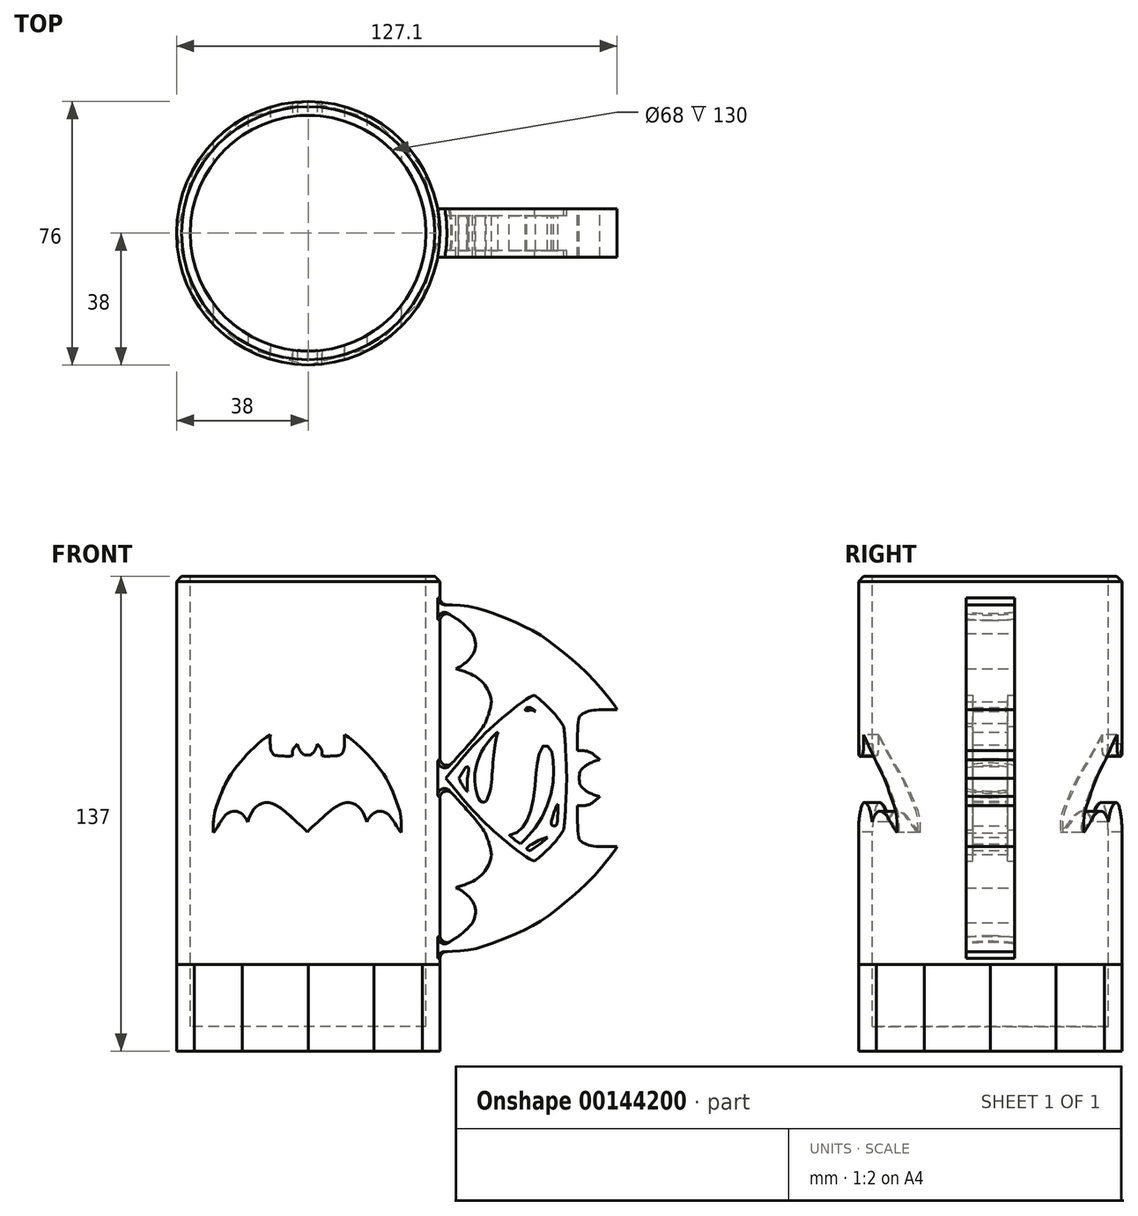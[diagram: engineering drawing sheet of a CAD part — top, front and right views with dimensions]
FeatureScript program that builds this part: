
annotation { "Feature Type Name" : "Feature", "Feature Type Description" : "" }
export const myFeature = defineFeature(function(context is Context, id is Id, definition is map)
    precondition{}
    {
        {
            var Q0;
            Q0=qCreatedBy(makeId("Top.planeOp"),FACE);
            var sketch = newSketch(context, id + "F0", { "sketchPlane" : qUnion([Q0])});
            skCircle(sketch, "E0", {"center": v(0, 0) * mm, "radius": 38 * mm});
            skSolve(sketch);
        }
        {
            var Q0;
            Q0=qSketchRegion(id+"F0",true);
            extrude(context, id + "F1", {"entities" : qUnion([Q0]), "depth" : 137 * mm});
        }
        {
            var Q0;
            Q0=makeQuery(id+"F1.opExtrude","CAP_FACE",FACE,{"disambiguationData":[OSD([sQuery(id+"F0.wireOp",EDGE,"E0")])],"isStart":false});
            var sketch = newSketch(context, id + "F2", { "sketchPlane" : qUnion([Q0])});
            skCircle(sketch, "E1", {"center": v(0, 0) * mm, "radius": 34 * mm});
            skSolve(sketch);
        }
        {
            var Q0;
            Q0=qSketchRegion(id+"F2",true);
            extrude(context, id + "F3", {"entities" : qUnion([Q0]), "operationType" : NewBodyOperationType.REMOVE, "oppositeDirection" : true, "depth" : 130 * mm});
        }
        {
            var Q0;
            Q0=qCreatedBy(makeId("Front.planeOp"),FACE);
            var sketch = newSketch(context, id + "F4", { "sketchPlane" : qUnion([Q0])});
            skFitSpline(sketch, "E2", {"points": [v(36.9, 128.73) * mm, v(42.12, 128.73) * mm, v(47.93, 128) * mm, v(54.17, 125.97) * mm, v(60.56, 123.36) * mm, v(67.67, 119.58) * mm, v(74.93, 113.92) * mm, v(82.05, 107.39) * mm, v(88.87, 98.97) * mm, v(89.1, 98.44) * mm], "startDerivative": vector(51.79, 1.09) * mm, "endDerivative": vector(2.7, -11.12) * mm});
            skFitSpline(sketch, "E3", {"points": [v(89.1, 98.44) * mm, v(83.25, 98.44) * mm, v(80.58, 97.98) * mm, v(78.7, 96.95) * mm, v(78.04, 95.83) * mm, v(77.66, 86.63) * mm], "startDerivative": vector(-27.8, 0.53) * mm, "endDerivative": vector(0.96, -37) * mm});
            skFitSpline(sketch, "E4", {"points": [v(77.66, 86.63) * mm, v(79.5, 86.63) * mm, v(81.03, 86.36) * mm, v(82.92, 85.1) * mm, v(84.15, 84.06) * mm], "startDerivative": vector(6.72, 0.3) * mm, "endDerivative": vector(4.9, -4.18) * mm});
            skFitSpline(sketch, "E5", {"points": [v(84.15, 84.06) * mm, v(81.63, 83.24) * mm, v(79.99, 82.28) * mm, v(78.53, 80.8) * mm, v(78.19, 78.74) * mm], "startDerivative": vector(-7.25, -1.04) * mm, "endDerivative": vector(-0.08, -9.17) * mm});
            skFitSpline(sketch, "E6", {"points": [v(36.9, 128.73) * mm, v(43.3, 124.4) * mm, v(46.88, 121.41) * mm, v(48.14, 116) * mm, v(44.69, 111.5) * mm, v(42.61, 110.37) * mm], "startDerivative": vector(16.64, -13.44) * mm, "endDerivative": vector(-14.87, -5.9) * mm});
            skFitSpline(sketch, "E7", {"points": [v(42.61, 110.37) * mm, v(44.83, 109.6) * mm, v(49.77, 106.88) * mm, v(52.87, 100.78) * mm, v(51.04, 94.56) * mm, v(44.19, 86.1) * mm, v(39.39, 80.85) * mm, v(37.25, 78.74) * mm], "startDerivative": vector(23.87, -9.84) * mm, "endDerivative": vector(-19.45, -17.88) * mm});
            skLineSegment(sketch, "E8", {"start": v(33.29, 78.74) * mm, "end": v(88.65, 78.74) * mm, "construction": true});
            skFitSpline(sketch, "E9.MirrorCS", {"points": [v(84.15, 73.42) * mm, v(81.63, 74.24) * mm, v(79.99, 75.2) * mm, v(78.53, 76.68) * mm, v(78.19, 78.74) * mm], "startDerivative": vector(-7.25, 1.04) * mm, "endDerivative": vector(-0.08, 9.17) * mm});
            skFitSpline(sketch, "E10.MirrorCS", {"points": [v(77.66, 70.85) * mm, v(79.5, 70.85) * mm, v(81.03, 71.13) * mm, v(82.92, 72.4) * mm, v(84.15, 73.42) * mm], "startDerivative": vector(6.72, -0.3) * mm, "endDerivative": vector(4.9, 4.18) * mm});
            skFitSpline(sketch, "E11.MirrorCS", {"points": [v(89.1, 59.04) * mm, v(83.25, 59.04) * mm, v(80.58, 59.5) * mm, v(78.7, 60.53) * mm, v(78.04, 61.65) * mm, v(77.66, 70.85) * mm], "startDerivative": vector(-27.8, -0.53) * mm, "endDerivative": vector(0.96, 37) * mm});
            skFitSpline(sketch, "E12.MirrorCS", {"points": [v(36.9, 28.75) * mm, v(42.12, 28.75) * mm, v(47.93, 29.48) * mm, v(54.17, 31.51) * mm, v(60.56, 34.12) * mm, v(67.67, 37.9) * mm, v(74.93, 43.56) * mm, v(82.05, 50.1) * mm, v(88.87, 58.52) * mm, v(89.1, 59.04) * mm], "startDerivative": vector(51.79, -1.09) * mm, "endDerivative": vector(2.7, 11.12) * mm});
            skFitSpline(sketch, "E13.MirrorCS", {"points": [v(36.9, 28.75) * mm, v(43.3, 33.07) * mm, v(46.88, 36.07) * mm, v(48.14, 41.49) * mm, v(44.69, 45.98) * mm, v(42.61, 47.12) * mm], "startDerivative": vector(16.64, 13.44) * mm, "endDerivative": vector(-14.87, 5.9) * mm});
            skFitSpline(sketch, "E14.MirrorCS", {"points": [v(42.61, 47.12) * mm, v(44.83, 47.89) * mm, v(49.77, 50.6) * mm, v(52.87, 56.7) * mm, v(51.04, 62.92) * mm, v(44.19, 71.4) * mm, v(39.39, 76.63) * mm, v(37.25, 78.74) * mm], "startDerivative": vector(23.87, 9.84) * mm, "endDerivative": vector(-19.45, 17.88) * mm});
            skLineSegment(sketch, "E15", {"start": v(64.5, 49.68) * mm, "end": v(64.5, 113.06) * mm, "construction": true});
            skFitSpline(sketch, "E16", {"points": [v(74.58, 78.74) * mm, v(74.04, 90.2) * mm, v(73.7, 93.64) * mm], "startDerivative": vector(-0.8, 20.33) * mm, "endDerivative": vector(-0.95, 8.3) * mm});
            skFitSpline(sketch, "E17", {"points": [v(73.7, 93.64) * mm, v(70.4, 98.01) * mm, v(65.3, 102.65) * mm], "startDerivative": vector(-6.4, 9.4) * mm, "endDerivative": vector(-3.05, 1.66) * mm});
            skFitSpline(sketch, "E18", {"points": [v(65.3, 102.65) * mm, v(59.66, 99.1) * mm, v(49.84, 90.46) * mm, v(39.71, 78.74) * mm], "startDerivative": vector(-13.82, -2.57) * mm, "endDerivative": vector(-25.21, -31.02) * mm});
            skFitSpline(sketch, "E19", {"points": [v(45.95, 74.86) * mm, v(45.9, 78.74) * mm, v(46.28, 81.04) * mm, v(45.73, 82.1) * mm], "startDerivative": vector(-0.69, 9.3) * mm, "endDerivative": vector(-5.98, 2.33) * mm});
            skFitSpline(sketch, "E20", {"points": [v(45.73, 82.1) * mm, v(44.59, 80.57) * mm, v(43.51, 78.74) * mm], "startDerivative": vector(-3.02, -2.78) * mm, "endDerivative": vector(-1.95, -3.79) * mm});
            skFitSpline(sketch, "E21", {"points": [v(43.51, 78.74) * mm, v(44.28, 77.1) * mm, v(45.08, 75.82) * mm, v(45.95, 74.86) * mm], "startDerivative": vector(0.56, -4.35) * mm, "endDerivative": vector(2.23, -1.28) * mm});
            skFitSpline(sketch, "E22.MirrorCS", {"points": [v(74.58, 78.74) * mm, v(74.04, 67.3) * mm, v(73.7, 63.85) * mm], "startDerivative": vector(-0.8, -20.33) * mm, "endDerivative": vector(-0.95, -8.3) * mm});
            skFitSpline(sketch, "E23.MirrorCS", {"points": [v(73.7, 63.85) * mm, v(70.4, 59.47) * mm, v(65.3, 54.83) * mm], "startDerivative": vector(-6.4, -9.4) * mm, "endDerivative": vector(-3.05, -1.66) * mm});
            skFitSpline(sketch, "E24.MirrorCS", {"points": [v(65.3, 54.83) * mm, v(59.66, 58.4) * mm, v(49.84, 67.02) * mm, v(39.71, 78.74) * mm], "startDerivative": vector(-13.82, 2.57) * mm, "endDerivative": vector(-25.21, 31.02) * mm});
            skFitSpline(sketch, "E25", {"points": [v(54.78, 92.08) * mm, v(54.1, 89.74) * mm, v(53.36, 83.81) * mm, v(52.59, 75.72) * mm, v(51.31, 72.04) * mm], "startDerivative": vector(-3.91, -11.71) * mm, "endDerivative": vector(-7.77, -13.72) * mm});
            skFitSpline(sketch, "E26", {"points": [v(51.31, 72.04) * mm, v(50.45, 71.85) * mm, v(49.56, 72.25) * mm, v(48.61, 74.4) * mm, v(48.12, 77.19) * mm, v(48.12, 80.34) * mm, v(49.23, 84.76) * mm, v(51.7, 89) * mm, v(53.85, 91.39) * mm, v(54.78, 92.08) * mm], "startDerivative": vector(-12.82, -4.34) * mm, "endDerivative": vector(11.18, 7.53) * mm});
            skFitSpline(sketch, "E27", {"points": [v(65.56, 98.05) * mm, v(64.5, 98.4) * mm, v(63.24, 98.23) * mm, v(62.59, 98.42) * mm, v(63.64, 99.17) * mm, v(65.56, 98.05) * mm]});
            skFitSpline(sketch, "E28", {"points": [v(72, 71.25) * mm, v(71.96, 68.06) * mm, v(71.7, 65.44) * mm, v(71.02, 64.97) * mm, v(70.23, 65.23) * mm, v(70.71, 68.28) * mm, v(72, 71.25) * mm]});
            skFitSpline(sketch, "E29", {"points": [v(68.95, 61.62) * mm, v(66.19, 59.31) * mm, v(64.16, 57.89) * mm, v(63.51, 57.95) * mm, v(63.07, 58.36) * mm, v(63.99, 59.34) * mm, v(66.8, 60.93) * mm, v(68.95, 61.62) * mm]});
            skFitSpline(sketch, "E30", {"points": [v(61.22, 59.77) * mm, v(60.27, 60.5) * mm, v(57.96, 62.14) * mm, v(59.38, 62.77) * mm, v(61.38, 64.03) * mm, v(62.75, 65.82) * mm, v(64.04, 68.72) * mm, v(65.11, 73.92) * mm, v(65.72, 80.16) * mm, v(66.14, 83.44) * mm, v(66.95, 86.55) * mm, v(68.14, 88.3) * mm, v(69.2, 87.92) * mm, v(70.19, 86.6) * mm, v(70.64, 84.34) * mm, v(70.77, 80.26) * mm, v(70.27, 75.47) * mm, v(68.59, 70.03) * mm, v(66.14, 65.32) * mm, v(61.88, 60.3) * mm, v(61.22, 59.77) * mm]});
            skLineSegment(sketch, "E31", {"start": v(0, 0) * mm, "end": v(0, 137) * mm, "construction": true});
            skLineSegment(sketch, "E32", {"start": v(0, 137) * mm, "end": v(38, 137) * mm, "construction": true});
            skLineSegment(sketch, "E33", {"start": v(38, 137) * mm, "end": v(38, 117) * mm, "construction": true});
            skArc(sketch, "E34", {"start": v(51.04, 94.56) * mm, "mid": v(52.37, 110.83) * mm, "end": v(43.3, 124.4) * mm});
            skArc(sketch, "E35", {"start": v(43.3, 33.07) * mm, "mid": v(52.37, 46.65) * mm, "end": v(51.04, 62.92) * mm});
            skSolve(sketch);
        }
        {
            var Q0;
            Q0=qSketchRegion(id+"F4",true);
            extrude(context, id + "F5", {"entities" : qUnion([Q0]), "operationType" : NewBodyOperationType.ADD, "endBound" : BoundingType.SYMMETRIC, "depth" : 14 * mm});
        }
        {
            var Q0;
            Q0=makeQuery(id+"F4.imprint","IMPRINT",FACE,{"disambiguationData":[TD([[makeQuery(id+"F4.imprint","IMPRINT",EDGE,{"derivedFrom":sQuery(id+"F4.wireOp",EDGE,"E16")}),1.0]])]});
            extrude(context, id + "F6", {"entities" : qUnion([Q0]), "operationType" : NewBodyOperationType.ADD, "endBound" : BoundingType.SYMMETRIC, "depth" : 10 * mm});
        }
        {
            var Q0;
            Q0=makeQuery(id+"F5.boolean.opBoolean","INTERSECT",EDGE,{"derivedFrom":[makeQuery(id+"F1.opExtrude","SWEPT_FACE",FACE,{"disambiguationData":[OSD([sQuery(id+"F0.wireOp",EDGE,"E0")])]}),makeQuery(id+"F5.opExtrude","SWEPT_FACE",FACE,{"disambiguationData":[OSD([sQuery(id+"F4.wireOp",EDGE,"E2")])]})]});
            var Q1;
            Q1=makeQuery(id+"F5.boolean.opBoolean","INTERSECT",EDGE,{"derivedFrom":[makeQuery(id+"F1.opExtrude","SWEPT_FACE",FACE,{"disambiguationData":[OSD([sQuery(id+"F0.wireOp",EDGE,"E0")])]}),makeQuery(id+"F5.opExtrude","SWEPT_FACE",FACE,{"disambiguationData":[OSD([sQuery(id+"F4.wireOp",EDGE,"E6")])]})]});
            var Q2;
            Q2=makeQuery(id+"F5.boolean.opBoolean","INTERSECT",EDGE,{"derivedFrom":[makeQuery(id+"F1.opExtrude","SWEPT_FACE",FACE,{"disambiguationData":[OSD([sQuery(id+"F0.wireOp",EDGE,"E0")])]}),makeQuery(id+"F5.opExtrude","SWEPT_FACE",FACE,{"disambiguationData":[OSD([sQuery(id+"F4.wireOp",EDGE,"E13.MirrorCS")])]})]});
            var Q3;
            Q3=makeQuery(id+"F5.boolean.opBoolean","INTERSECT",EDGE,{"derivedFrom":[makeQuery(id+"F1.opExtrude","SWEPT_FACE",FACE,{"disambiguationData":[OSD([sQuery(id+"F0.wireOp",EDGE,"E0")])]}),makeQuery(id+"F5.opExtrude","SWEPT_FACE",FACE,{"disambiguationData":[OSD([sQuery(id+"F4.wireOp",EDGE,"E14.MirrorCS")])]})]});
            var Q4;
            Q4=makeQuery(id+"F5.boolean.opBoolean","INTERSECT",EDGE,{"derivedFrom":[makeQuery(id+"F1.opExtrude","SWEPT_FACE",FACE,{"disambiguationData":[OSD([sQuery(id+"F0.wireOp",EDGE,"E0")])]}),makeQuery(id+"F5.opExtrude","SWEPT_FACE",FACE,{"disambiguationData":[OSD([sQuery(id+"F4.wireOp",EDGE,"E12.MirrorCS")])]})]});
            var Q5;
            Q5=makeQuery(id+"F5.boolean.opBoolean","INTERSECT",EDGE,{"derivedFrom":[makeQuery(id+"F1.opExtrude","SWEPT_FACE",FACE,{"disambiguationData":[OSD([sQuery(id+"F0.wireOp",EDGE,"E0")])]}),makeQuery(id+"F5.opExtrude","SWEPT_FACE",FACE,{"disambiguationData":[OSD([sQuery(id+"F4.wireOp",EDGE,"E7")])]})]});
            fillet(context, id + "F7", {"entities" : qUnion([Q0, Q1, Q2, Q3, Q4, Q5]), "radius" : 2 * mm, "tangentPropagation" : true, "allowEdgeOverflow" : false});
        }
        {
            var Q0;
            Q0=makeQuery(id+"F1.opExtrude","CAP_EDGE",EDGE,{"disambiguationData":[OSD([sQuery(id+"F0.wireOp",EDGE,"E0")])],"isStart":false});
            chamfer(context, id + "F8", {"entities" : qUnion([Q0]), "width" : 1.5 * mm, "tangentPropagation" : true});
        }
        {
            var Q0;
            Q0=makeQuery(id+"F1.opExtrude","CAP_FACE",FACE,{"disambiguationData":[OSD([sQuery(id+"F0.wireOp",EDGE,"E0")])],"isStart":true});
            var sketch = newSketch(context, id + "F9", { "sketchPlane" : qUnion([Q0])});
            skLineSegment(sketch, "E36", {"start": v(0, 38) * mm, "end": v(0, 0) * mm, "construction": true});
            skLineSegment(sketch, "E37", {"start": v(0, 0) * mm, "end": v(-38, 0) * mm, "construction": true});
            skLineSegment(sketch, "E38", {"start": v(0, 0) * mm, "end": v(-32.9, 19) * mm, "construction": true});
            skLineSegment(sketch, "E39", {"start": v(-38, 0) * mm, "end": v(-32.9, 19) * mm});
            skLineSegment(sketch, "E40.1.0", {"start": v(-32.9, -19) * mm, "end": v(-38, 0) * mm});
            skLineSegment(sketch, "E40.2.0", {"start": v(-19, -32.9) * mm, "end": v(-32.9, -19) * mm});
            skLineSegment(sketch, "E40.3.0", {"start": v(0, -38) * mm, "end": v(-19, -32.9) * mm});
            skLineSegment(sketch, "E40.4.0", {"start": v(19, -32.9) * mm, "end": v(0, -38) * mm});
            skLineSegment(sketch, "E40.5.0", {"start": v(32.9, -19) * mm, "end": v(19, -32.9) * mm});
            skLineSegment(sketch, "E40.6.0", {"start": v(38, 0) * mm, "end": v(32.9, -19) * mm});
            skLineSegment(sketch, "E40.7.0", {"start": v(32.9, 19) * mm, "end": v(38, 0) * mm});
            skLineSegment(sketch, "E40.8.0", {"start": v(19, 32.9) * mm, "end": v(32.9, 19) * mm});
            skLineSegment(sketch, "E40.9.0", {"start": v(0, 38) * mm, "end": v(19, 32.9) * mm});
            skLineSegment(sketch, "E40.10.0", {"start": v(-19, 32.9) * mm, "end": v(0, 38) * mm});
            skLineSegment(sketch, "E40.11.0", {"start": v(-32.9, 19) * mm, "end": v(-19, 32.9) * mm});
            skPoint(sketch, "E40.center", {"position": v(0, 0) * mm});
            skLineSegment(sketch, "E41", {"start": v(0, 0) * mm, "end": v(-19, 32.9) * mm, "construction": true});
            skSolve(sketch);
        }
        {
            var Q0;
            {var subQ0=sQuery(id+"F9.wireOp",EDGE,"E40.11.0");Q0=makeQuery(id+"F9.imprint","IMPRINT",FACE,{"disambiguationData":[TD([[makeQuery(id+"F9.imprint","IMPRINT",EDGE,{"derivedFrom":subQ0}),1.0]])]});}
            var Q1;
            {var subQ0=sQuery(id+"F9.wireOp",EDGE,"E39");Q1=makeQuery(id+"F9.imprint","IMPRINT",FACE,{"disambiguationData":[TD([[makeQuery(id+"F9.imprint","IMPRINT",EDGE,{"derivedFrom":subQ0}),1.0]])]});}
            var Q2;
            {var subQ0=sQuery(id+"F9.wireOp",EDGE,"E40.10.0");Q2=makeQuery(id+"F9.imprint","IMPRINT",FACE,{"disambiguationData":[TD([[makeQuery(id+"F9.imprint","IMPRINT",EDGE,{"derivedFrom":subQ0}),1.0]])]});}
            var Q3;
            {var subQ0=sQuery(id+"F9.wireOp",EDGE,"E40.9.0");Q3=makeQuery(id+"F9.imprint","IMPRINT",FACE,{"disambiguationData":[TD([[makeQuery(id+"F9.imprint","IMPRINT",EDGE,{"derivedFrom":subQ0}),1.0]])]});}
            var Q4;
            {var subQ0=sQuery(id+"F9.wireOp",EDGE,"E40.8.0");Q4=makeQuery(id+"F9.imprint","IMPRINT",FACE,{"disambiguationData":[TD([[makeQuery(id+"F9.imprint","IMPRINT",EDGE,{"derivedFrom":subQ0}),1.0]])]});}
            var Q5;
            {var subQ0=sQuery(id+"F9.wireOp",EDGE,"E40.7.0");Q5=makeQuery(id+"F9.imprint","IMPRINT",FACE,{"disambiguationData":[TD([[makeQuery(id+"F9.imprint","IMPRINT",EDGE,{"derivedFrom":subQ0}),1.0]])]});}
            var Q6;
            {var subQ0=sQuery(id+"F9.wireOp",EDGE,"E40.6.0");Q6=makeQuery(id+"F9.imprint","IMPRINT",FACE,{"disambiguationData":[TD([[makeQuery(id+"F9.imprint","IMPRINT",EDGE,{"derivedFrom":subQ0}),1.0]])]});}
            var Q7;
            {var subQ0=sQuery(id+"F9.wireOp",EDGE,"E40.5.0");Q7=makeQuery(id+"F9.imprint","IMPRINT",FACE,{"disambiguationData":[TD([[makeQuery(id+"F9.imprint","IMPRINT",EDGE,{"derivedFrom":subQ0}),1.0]])]});}
            var Q8;
            {var subQ0=sQuery(id+"F9.wireOp",EDGE,"E40.4.0");Q8=makeQuery(id+"F9.imprint","IMPRINT",FACE,{"disambiguationData":[TD([[makeQuery(id+"F9.imprint","IMPRINT",EDGE,{"derivedFrom":subQ0}),1.0]])]});}
            var Q9;
            {var subQ0=sQuery(id+"F9.wireOp",EDGE,"E40.3.0");Q9=makeQuery(id+"F9.imprint","IMPRINT",FACE,{"disambiguationData":[TD([[makeQuery(id+"F9.imprint","IMPRINT",EDGE,{"derivedFrom":subQ0}),1.0]])]});}
            var Q10;
            {var subQ0=sQuery(id+"F9.wireOp",EDGE,"E40.2.0");Q10=makeQuery(id+"F9.imprint","IMPRINT",FACE,{"disambiguationData":[TD([[makeQuery(id+"F9.imprint","IMPRINT",EDGE,{"derivedFrom":subQ0}),1.0]])]});}
            var Q11;
            {var subQ0=sQuery(id+"F9.wireOp",EDGE,"E40.1.0");Q11=makeQuery(id+"F9.imprint","IMPRINT",FACE,{"disambiguationData":[TD([[makeQuery(id+"F9.imprint","IMPRINT",EDGE,{"derivedFrom":subQ0}),1.0]])]});}
            extrude(context, id + "F10", {"entities" : qUnion([Q0, Q1, Q2, Q3, Q4, Q5, Q6, Q7, Q8, Q9, Q10, Q11]), "operationType" : NewBodyOperationType.REMOVE, "oppositeDirection" : true, "depth" : 25 * mm});
        }
        {
            var Q0;
            Q0=qCreatedBy(makeId("Front.planeOp"),FACE);
            cPlane(context, id + "F11", {"entities" : qUnion([Q0]), "cplaneType" : CPlaneType.OFFSET, "offset" : (76 / 2) * mm, "width" : 150 * mm, "height" : 150 * mm});
        }
        {
            var Q0;
            Q0=qCreatedBy(id+"F11.planeOp",FACE);
            var sketch = newSketch(context, id + "F12", { "sketchPlane" : qUnion([Q0])});
            skFitSpline(sketch, "E42", {"points": [v(-27.35, 63.02) * mm, v(-27.35, 65.86) * mm, v(-26.95, 69) * mm, v(-25.85, 72.39) * mm, v(-24.44, 75.85) * mm, v(-22.4, 79.7) * mm, v(-19.32, 83.64) * mm, v(-15.78, 87.5) * mm, v(-11.22, 91.19) * mm, v(-10.94, 91.31) * mm], "startDerivative": vector(-0.59, 28.06) * mm, "endDerivative": vector(6.03, 1.46) * mm});
            skFitSpline(sketch, "E43", {"points": [v(-10.94, 91.31) * mm, v(-10.94, 88.14) * mm, v(-10.68, 86.7) * mm, v(-10.13, 85.68) * mm, v(-9.52, 85.32) * mm, v(-4.54, 85.12) * mm], "startDerivative": vector(-0.29, -15.07) * mm, "endDerivative": vector(20.05, 0.52) * mm});
            skFitSpline(sketch, "E44", {"points": [v(-4.54, 85.12) * mm, v(-4.54, 86.1) * mm, v(-4.39, 86.94) * mm, v(-3.7, 87.96) * mm, v(-3.14, 88.63) * mm], "startDerivative": vector(-0.16, 3.64) * mm, "endDerivative": vector(2.26, 2.66) * mm});
            skFitSpline(sketch, "E45", {"points": [v(-3.14, 88.63) * mm, v(-2.7, 87.27) * mm, v(-2.18, 86.38) * mm, v(-1.38, 85.59) * mm, v(-0.26, 85.4) * mm], "startDerivative": vector(0.56, -3.93) * mm, "endDerivative": vector(4.97, -0.04) * mm});
            skFitSpline(sketch, "E46", {"points": [v(-27.35, 63.02) * mm, v(-25, 66.5) * mm, v(-23.38, 68.43) * mm, v(-20.45, 69.12) * mm, v(-18.01, 67.25) * mm, v(-17.4, 66.12) * mm], "startDerivative": vector(7.28, 9.02) * mm, "endDerivative": vector(3.2, -8.06) * mm});
            skFitSpline(sketch, "E47", {"points": [v(-17.4, 66.12) * mm, v(-16.98, 67.32) * mm, v(-15.5, 70) * mm, v(-12.2, 71.68) * mm, v(-8.83, 70.7) * mm, v(-4.24, 66.98) * mm, v(-1.4, 64.37) * mm, v(-0.26, 63.22) * mm], "startDerivative": vector(5.33, 12.94) * mm, "endDerivative": vector(9.7, -10.54) * mm});
            skLineSegment(sketch, "E48", {"start": v(-0.26, 61.07) * mm, "end": v(-0.26, 91.07) * mm, "construction": true});
            skFitSpline(sketch, "E49.MirrorCS", {"points": [v(2.62, 88.63) * mm, v(2.18, 87.27) * mm, v(1.66, 86.38) * mm, v(0.86, 85.59) * mm, v(-0.26, 85.4) * mm], "startDerivative": vector(-0.56, -3.93) * mm, "endDerivative": vector(-4.97, -0.04) * mm});
            skFitSpline(sketch, "E50.MirrorCS", {"points": [v(4.02, 85.12) * mm, v(4.02, 86.1) * mm, v(3.87, 86.94) * mm, v(3.18, 87.96) * mm, v(2.62, 88.63) * mm], "startDerivative": vector(0.16, 3.64) * mm, "endDerivative": vector(-2.26, 2.66) * mm});
            skFitSpline(sketch, "E51.MirrorCS", {"points": [v(10.42, 91.31) * mm, v(10.42, 88.14) * mm, v(10.17, 86.7) * mm, v(9.6, 85.68) * mm, v(9, 85.32) * mm, v(4.02, 85.12) * mm], "startDerivative": vector(0.29, -15.07) * mm, "endDerivative": vector(-20.05, 0.52) * mm});
            skFitSpline(sketch, "E52.MirrorCS", {"points": [v(26.83, 63.02) * mm, v(26.83, 65.86) * mm, v(26.43, 69) * mm, v(25.33, 72.39) * mm, v(23.92, 75.85) * mm, v(21.87, 79.7) * mm, v(18.8, 83.64) * mm, v(15.26, 87.5) * mm, v(10.7, 91.19) * mm, v(10.42, 91.31) * mm], "startDerivative": vector(0.59, 28.06) * mm, "endDerivative": vector(-6.03, 1.46) * mm});
            skFitSpline(sketch, "E53.MirrorCS", {"points": [v(26.83, 63.02) * mm, v(24.49, 66.5) * mm, v(22.86, 68.43) * mm, v(19.93, 69.12) * mm, v(17.5, 67.25) * mm, v(16.88, 66.12) * mm], "startDerivative": vector(-7.28, 9.02) * mm, "endDerivative": vector(-3.2, -8.06) * mm});
            skFitSpline(sketch, "E54.MirrorCS", {"points": [v(16.88, 66.12) * mm, v(16.46, 67.32) * mm, v(14.99, 70) * mm, v(11.68, 71.68) * mm, v(8.31, 70.7) * mm, v(3.72, 66.98) * mm, v(0.88, 64.37) * mm, v(-0.26, 63.22) * mm], "startDerivative": vector(-5.33, 12.94) * mm, "endDerivative": vector(-9.7, -10.54) * mm});
            skLineSegment(sketch, "E55", {"start": v(15.49, 77.98) * mm, "end": v(-18.86, 77.98) * mm, "construction": true});
            skSolve(sketch);
        }
        {
            var Q0;
            Q0=makeQuery(id+"F12.imprint","IMPRINT",FACE,{"disambiguationData":[TD([[makeQuery(id+"F12.imprint","IMPRINT",EDGE,{"derivedFrom":sQuery(id+"F12.wireOp",EDGE,"E42")}),-1.0]])]});
            extrude(context, id + "F13", {"entities" : qUnion([Q0]), "operationType" : NewBodyOperationType.REMOVE, "endBound" : BoundingType.THROUGH_ALL, "oppositeDirection" : true, "depth" : 25 * mm});
        }
    });
